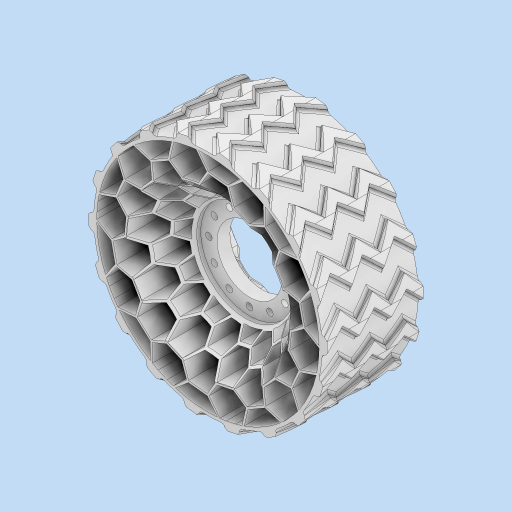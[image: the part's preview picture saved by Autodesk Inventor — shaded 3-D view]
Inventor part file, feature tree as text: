
AUTODESK INVENTOR PART (.ipt)
format: ipt  version: 2023 (Build 270158000, 158)  size: 2,840,064 bytes
history: native  units: in
note: dims shown in document units (in); Inventor stores cm internally (conversion verified against a paired STEP export)
features: extrude x21, thicken_offset x17, other x17, sketch x5, pattern_circular x2, plane x2, fillet x2, chamfer x2, mirror x1, sweep x1, projected_geometry x1
ambient origin geometry x8: Origin, YZ Plane, XZ Plane, XY Plane, X Axis, Y Axis, Z Axis, Center Point
bodies: Solid1 (feature_tree)
feature tree (71):
  sketch  "Sketch1"  dims[d0=2.9528in d1=0.0in d2=2.9528in d3=0.0in]
  extrude  "Extrusion1"  Depth=2.9528in TaperAngle=0.0deg
  thicken_offset  "Thicken1"
  thicken_offset  "Thicken2"
  thicken_offset  "Thicken3"
  thicken_offset  "Thicken4"
  thicken_offset  "Thicken5"
  thicken_offset  "Thicken6"
  thicken_offset  "Thicken7"
  thicken_offset  "Thicken8"
  thicken_offset  "Thicken9"
  thicken_offset  "Thicken10"
  thicken_offset  "Thicken11"
  thicken_offset  "Thicken12"
  thicken_offset  "Thicken13"
  thicken_offset  "Thicken14"
  thicken_offset  "Thicken15"
  thicken_offset  "Thicken16"
  thicken_offset  "Thicken17"
  pattern_circular  "Circular Pattern1"  [2 undecoded]
  sketch  "Sketch2"  dims[d4=0.0945in]
  extrude  "Extrusion2"  Depth=2.9528in TaperAngle=0.0deg
  extrude  "Extrusion3"  Depth=0.063in
  plane  "Work Plane1"
  mirror  "Mirror1"
  plane  "Work Plane2"
  sweep  "Sweep1"
  extrude  "Extrusion4"  Depth=0.063in
  fillet  "Fillet2"  Radius=2.9528in
  pattern_circular  "Circular Pattern2"  [2 undecoded]
  fillet  "Fillet1"  Radius=2.9528in
  chamfer  "Chamfer1"  Distance=0.063in
  chamfer  "Chamfer2"  Distance=2.9528in
  other  "Srf1"
  other  "Srf2"
  other  "Srf3"
  other  "Srf4"
  other  "Srf5"
  other  "Srf6"
  other  "Srf7"
  other  "Srf8"
  other  "Srf9"
  other  "Srf10"
  other  "Srf11"
  other  "Srf12"
  other  "Srf13"
  other  "Srf14"
  other  "Srf15"
  other  "Srf16"
  other  "Srf17"
  sketch  "Sketch3"  dims[d5=2.9528in d6=0.0in]
  sketch  "Sketch4"  dims[d7=0.063in]
  projected_geometry  "Projected Loop1"
  sketch  "Sketch5"  dims[d8=2.9528in d9=0.0in d10=0.063in d11=2.9528in d12=0.0in d13=0.063in d14=2.9528in d15=0.0in d16=0.063in d17=2.9528in d18=0.0in d19=0.063in d20=2.9528in d21=0.0in d22=0.063in d23=2.9528in d24=0.0in d25=0.063in d26=2.9528in d27=0.0in d28=0.063in d29=2.9528in d30=0.0in d31=0.063in d32=2.9528in d33=0.0in d34=0.063in d35=2.9528in d36=0.0in d37=0.063in d38=2.9528in d39=0.0in d40=0.063in d41=2.9528in d42=0.0in d43=0.063in d44=2.9528in d45=0.0in d46=0.063in d47=2.9528in d48=0.0in d49=0.063in d50=2.9528in d51=0.0in d52=0.063in d53=3.937in d54=360.0deg d57=4.7244in d58=2.5in d59=0.2057in d60=360.0deg d61=0.5in d62=3.0in d63=0.5in d64=0.0in d65=0.0in d66=1.2795in d67=0.0in d69=0.4724in d70=0.1575in d71=0.0787in d72=0.0787in d73=0.0787in d74=0.0787in d75=0.0in d76=0.0in d77=0.0in d78=0.0in d79=7.0866in d80=360.0deg d82=0.0039in d83=1.378in d84=1.0039in d85=1.1545in d86=45.0deg d87=1.0039in d88=1.1545in d89=45.0deg d90=0.0787in]
  extrude  "ExtrusionSrf1"  Depth=0.063in
  extrude  "ExtrusionSrf2"  Depth=2.9528in TaperAngle=0.0deg
  extrude  "ExtrusionSrf3"  Depth=0.063in
  extrude  "ExtrusionSrf4"  Depth=2.9528in TaperAngle=0.0deg
  extrude  "ExtrusionSrf5"  Depth=0.063in
  extrude  "ExtrusionSrf6"  Depth=2.9528in TaperAngle=0.0deg
  extrude  "ExtrusionSrf7"  Depth=0.063in
  extrude  "ExtrusionSrf8"  Depth=2.9528in TaperAngle=0.0deg
  extrude  "ExtrusionSrf9"  Depth=0.063in
  extrude  "ExtrusionSrf10"  Depth=2.9528in TaperAngle=0.0deg
  extrude  "ExtrusionSrf11"  Depth=0.063in
  extrude  "ExtrusionSrf12"  Depth=2.9528in TaperAngle=0.0deg
  extrude  "ExtrusionSrf13"  Depth=0.063in
  extrude  "ExtrusionSrf14"  Depth=2.9528in TaperAngle=0.0deg
  extrude  "ExtrusionSrf15"  Depth=0.063in
  extrude  "ExtrusionSrf16"  Depth=2.9528in TaperAngle=0.0deg
  extrude  "ExtrusionSrf17"  Depth=0.063in
note: 4 required parameter values undecoded (feature->parameter linkage not recoverable at this tier; creation-order binding heuristic only, values carry confidence <= 0.55)
